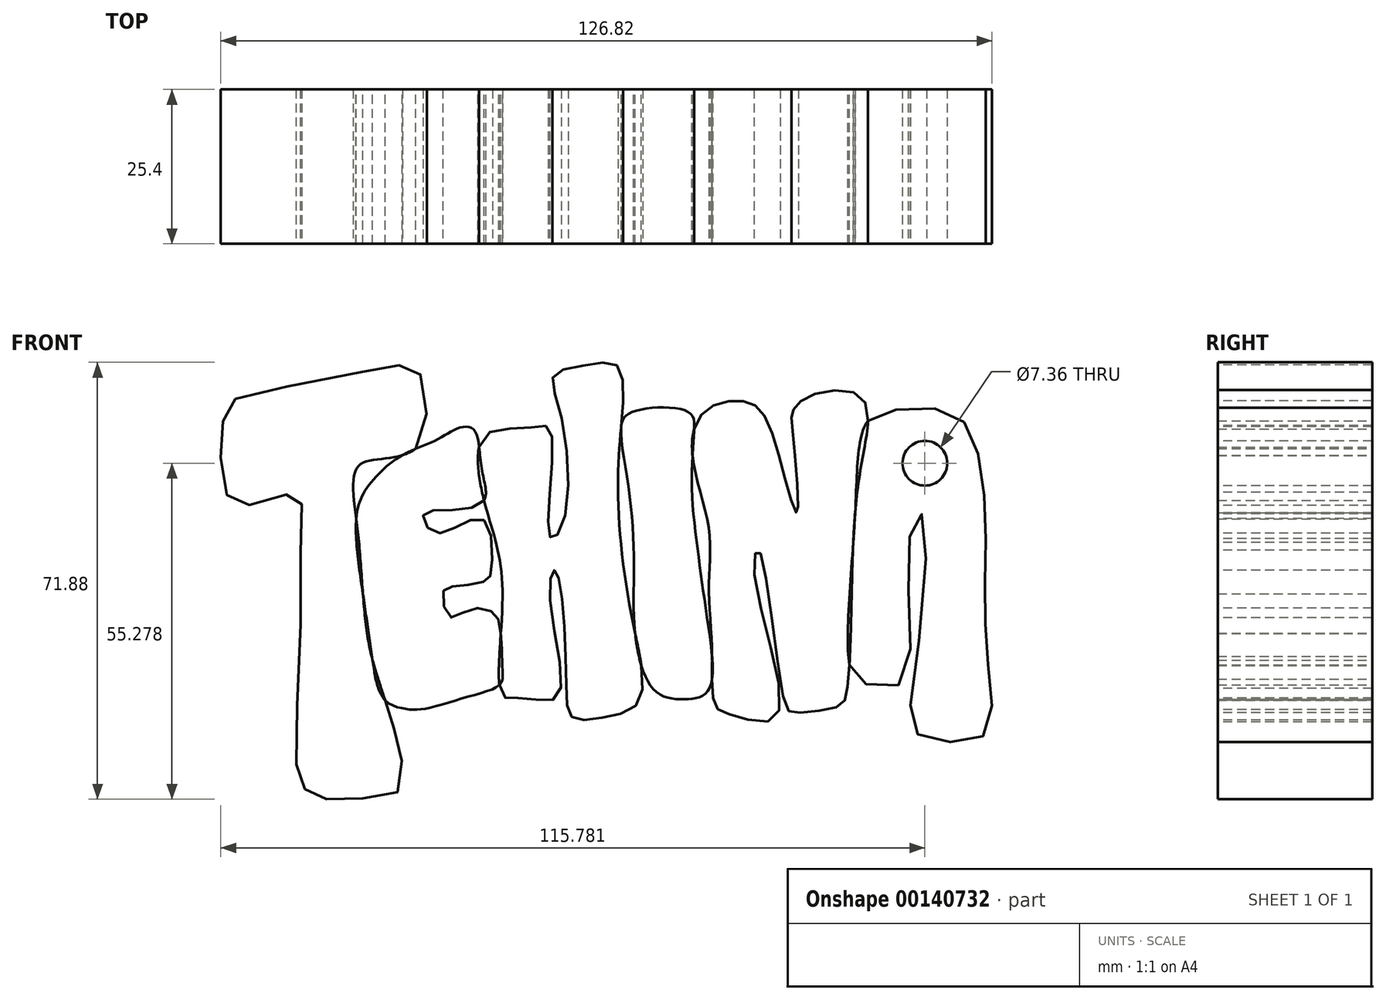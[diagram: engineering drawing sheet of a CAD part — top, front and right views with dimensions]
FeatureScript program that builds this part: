
annotation { "Feature Type Name" : "Feature", "Feature Type Description" : "" }
export const myFeature = defineFeature(function(context is Context, id is Id, definition is map)
    precondition{}
    {
        {
            var Q0;
            Q0=qCreatedBy(makeId("Front.planeOp"),FACE);
            var sketch = newSketch(context, id + "F0", { "sketchPlane" : qUnion([Q0])});
            skFitSpline(sketch, "E0", {"points": [v(-57.9, 25.8) * mm, v(-37.05, 29.96) * mm, v(-33.2, 30.6) * mm, v(-30.64, 30.12) * mm, v(-29.35, 25.47) * mm, v(-29.51, 18.25) * mm, v(-34.8, 15.37) * mm, v(-40.26, 13.92) * mm, v(-40.26, 3.02) * mm, v(-38.5, -15.02) * mm, v(-35.79, -24.54) * mm, v(-34.6, -28.44) * mm, v(-33.4, -31.84) * mm, v(-33.07, -37.89) * mm, v(-34.48, -40.11) * mm, v(-41.15, -40.72) * mm, v(-46, -40.72) * mm, v(-48.42, -39.7) * mm, v(-49.64, -38.1) * mm, v(-50.44, -33.85) * mm, v(-49.64, -10.61) * mm, v(-49.64, 6.16) * mm, v(-49.84, 9.6) * mm, v(-54.08, 8.58) * mm, v(-59.54, 7.57) * mm, v(-61.56, 8.79) * mm, v(-62.77, 14.44) * mm, v(-62.57, 20.5) * mm, v(-61.56, 24.14) * mm, v(-57.9, 25.8) * mm]});
            skFitSpline(sketch, "E1", {"points": [v(-27.4, 18.25) * mm, v(-23.57, 20.3) * mm, v(-21.15, 19.9) * mm, v(-19.93, 13.64) * mm, v(-19.53, 8.38) * mm, v(-24.98, 6.77) * mm, v(-29.51, 5.96) * mm, v(-27.81, 3.13) * mm, v(-23.37, 4.34) * mm, v(-19.33, 4.95) * mm, v(-18.32, -3.34) * mm, v(-19.33, -4.95) * mm, v(-24.18, -5.76) * mm, v(-26.2, -6.57) * mm, v(-25.19, -10.81) * mm, v(-21.95, -9.6) * mm, v(-18.11, -10) * mm, v(-16.9, -12.43) * mm, v(-16.5, -19.5) * mm, v(-16.9, -21.93) * mm, v(-22.16, -23.95) * mm, v(-29.51, -25.97) * mm, v(-32.26, -25.97) * mm, v(-35.79, -24.54) * mm, v(-37.85, -17.92) * mm, v(-39.44, -7.01) * mm, v(-40.54, 5.29) * mm, v(-38.5, 10.8) * mm, v(-32.97, 15.78) * mm, v(-27.4, 18.25) * mm]});
            skFitSpline(sketch, "E2", {"points": [v(-7, 22.93) * mm, v(-8.01, 29) * mm, v(-2.56, 30.6) * mm, v(2.3, 30.6) * mm, v(3.3, 24.14) * mm, v(2.5, 11.61) * mm, v(4.72, -10.61) * mm, v(5.93, -24.76) * mm, v(0, -27.38) * mm, v(-4.98, -27.38) * mm, v(-6, -22.13) * mm, v(-7, -5.76) * mm, v(-8.01, -3.14) * mm, v(-8.62, -8.6) * mm, v(-7.4, -23.95) * mm, v(-13.06, -24.15) * mm, v(-16.5, -23.75) * mm, v(-16.5, -5.96) * mm, v(-19.53, 8.38) * mm, v(-19.33, 19.1) * mm, v(-12.05, 20.3) * mm, v(-8.82, 20.3) * mm, v(-8.82, 8.38) * mm, v(-8.42, 2.12) * mm, v(-6.4, 4.95) * mm, v(-7, 22.93) * mm]});
            skFitSpline(sketch, "E3", {"points": [v(4.92, 22.93) * mm, v(3.02, 20.39) * mm, v(4.31, 10) * mm, v(5.12, -3.34) * mm, v(5.31, -13.5) * mm, v(8.56, -22.94) * mm, v(13.81, -24.35) * mm, v(17.45, -22.74) * mm, v(17.25, -11.62) * mm, v(15.63, 0) * mm, v(14.62, 11.41) * mm, v(15.02, 19.9) * mm, v(14.01, 22.93) * mm, v(4.92, 22.93) * mm]});
            skFitSpline(sketch, "E4", {"points": [v(16.64, 22.93) * mm, v(22.3, 24.75) * mm, v(26.14, 22.93) * mm, v(29.97, 11.82) * mm, v(32, 6.36) * mm, v(31.19, 19.9) * mm, v(31.19, 22.93) * mm, v(34.02, 25.56) * mm, v(42.5, 25.35) * mm, v(42.3, 13.03) * mm, v(40.89, -9) * mm, v(40.08, -23.54) * mm, v(38.66, -25.56) * mm, v(31.8, -26.57) * mm, v(29.97, -25.16) * mm, v(25.73, 0) * mm, v(24.92, -3.74) * mm, v(28.56, -27.18) * mm, v(21.29, -26.98) * mm, v(18.46, -25.36) * mm, v(17.97, -17.29) * mm, v(17.45, -5.36) * mm, v(17.45, 3.73) * mm, v(14.75, 15.73) * mm, v(16.64, 22.93) * mm]});
            skFitSpline(sketch, "E5", {"points": [v(43.6, 21.43) * mm, v(48.77, 23.33) * mm, v(57.05, 22.93) * mm, v(60.89, 18.69) * mm, v(62.7, 9.19) * mm, v(62.9, -2.13) * mm, v(62.9, -12.43) * mm, v(63.72, -22.13) * mm, v(63.11, -29.8) * mm, v(57.45, -31.42) * mm, v(51.4, -29.8) * mm, v(51.2, -20.71) * mm, v(52.6, 5.96) * mm, v(51.2, 5.15) * mm, v(50.38, -9.6) * mm, v(48.77, -21.93) * mm, v(42.9, -21.72) * mm, v(40.56, -18.67) * mm, v(41.5, 6.3) * mm, v(43.6, 21.43) * mm]});
            skSolve(sketch);
        }
        {
            var Q0;
            {var subQ0=sQuery(id+"F0.wireOp",EDGE,"E1");var subQ1=sQuery(id+"F0.wireOp",EDGE,"E0");var subQ7=makeQuery(id+"F0.imprint","INTERSECT",VERTEX,{"disambiguationData":[OD(2.0)],"derivedFrom":[subQ1,subQ0]});Q0=makeQuery(id+"F0.imprint","IMPRINT",FACE,{"disambiguationData":[TD([[makeQuery(id+"F0.imprint","IMPRINT",EDGE,{"disambiguationData":[TD([[subQ7,-1.0]])],"derivedFrom":subQ1}),-1.0]])]});}
            var Q1;
            Q1=sQuery(id+"F0.wireOp",EDGE,"E0");
            extrude(context, id + "F1", {"entities" : qUnion([Q0]), "surfaceEntities" : qUnion([Q1]), "depth" : 25.4 * mm});
        }
        {
            var Q0;
            {var subQ1=sQuery(id+"F0.wireOp",EDGE,"E1");var subQ4=sQuery(id+"F0.wireOp",EDGE,"E0");var subQ11=makeQuery(id+"F0.imprint","INTERSECT",VERTEX,{"disambiguationData":[OD(0.0)],"derivedFrom":[subQ4,subQ1]});Q0=makeQuery(id+"F0.imprint","IMPRINT",FACE,{"disambiguationData":[TD([[makeQuery(id+"F0.imprint","IMPRINT",EDGE,{"disambiguationData":[TD([[subQ11,-1.0]])],"derivedFrom":subQ4}),1.0]])]});}
            extrude(context, id + "F2", {"entities" : qUnion([Q0]), "depth" : 25.4 * mm});
        }
        {
            var Q0;
            {var subQ1=sQuery(id+"F0.wireOp",EDGE,"E2");var subQ4=sQuery(id+"F0.wireOp",EDGE,"E1");var subQ5=makeQuery(id+"F0.imprint","INTERSECT",VERTEX,{"disambiguationData":[OD(0.0)],"derivedFrom":[subQ4,subQ1]});Q0=makeQuery(id+"F0.imprint","IMPRINT",FACE,{"disambiguationData":[TD([[makeQuery(id+"F0.imprint","IMPRINT",EDGE,{"disambiguationData":[TD([[subQ5,-1.0]])],"derivedFrom":subQ4}),1.0]])]});}
            extrude(context, id + "F3", {"entities" : qUnion([Q0]), "depth" : 25.4 * mm});
        }
        {
            var Q0;
            {var subQ0=sQuery(id+"F0.wireOp",EDGE,"E3");var subQ1=sQuery(id+"F0.wireOp",EDGE,"E2");var subQ7=makeQuery(id+"F0.imprint","INTERSECT",VERTEX,{"disambiguationData":[OD(0.0)],"derivedFrom":[subQ1,subQ0]});Q0=makeQuery(id+"F0.imprint","IMPRINT",FACE,{"disambiguationData":[TD([[makeQuery(id+"F0.imprint","IMPRINT",EDGE,{"disambiguationData":[TD([[subQ7,-1.0]])],"derivedFrom":subQ1}),1.0]])]});}
            extrude(context, id + "F4", {"entities" : qUnion([Q0]), "depth" : 25.4 * mm});
        }
        {
            var Q0;
            {var subQ0=sQuery(id+"F0.wireOp",EDGE,"E4");var subQ1=sQuery(id+"F0.wireOp",EDGE,"E3");var subQ2=makeQuery(id+"F0.imprint","INTERSECT",VERTEX,{"disambiguationData":[OD(0.0)],"derivedFrom":[subQ1,subQ0]});Q0=makeQuery(id+"F0.imprint","IMPRINT",FACE,{"disambiguationData":[TD([[makeQuery(id+"F0.imprint","IMPRINT",EDGE,{"disambiguationData":[TD([[subQ2,-1.0]])],"derivedFrom":subQ1}),-1.0]])]});}
            extrude(context, id + "F5", {"entities" : qUnion([Q0]), "depth" : 25.4 * mm});
        }
        {
            var Q0;
            {var subQ0=sQuery(id+"F0.wireOp",EDGE,"E5");var subQ1=sQuery(id+"F0.wireOp",EDGE,"E4");var subQ2=makeQuery(id+"F0.imprint","INTERSECT",VERTEX,{"disambiguationData":[OD(0.0)],"derivedFrom":[subQ1,subQ0]});Q0=makeQuery(id+"F0.imprint","IMPRINT",FACE,{"disambiguationData":[TD([[makeQuery(id+"F0.imprint","IMPRINT",EDGE,{"disambiguationData":[TD([[subQ2,-1.0]])],"derivedFrom":subQ1}),1.0]])]});}
            extrude(context, id + "F6", {"entities" : qUnion([Q0]), "depth" : 25.4 * mm});
        }
        {
            var Q0;
            Q0=makeQuery(id+"F6.opExtrude","CAP_FACE",FACE,{"disambiguationData":[OSD([sQuery(id+"F0.wireOp",EDGE,"E4"),sQuery(id+"F0.wireOp",EDGE,"E5")])],"isStart":false});
            var sketch = newSketch(context, id + "F7", { "sketchPlane" : qUnion([Q0])});
            skCircle(sketch, "E6", {"center": v(52.96, 14.46) * mm, "radius": 3.68 * mm});
            skSolve(sketch);
        }
        {
            var Q0;
            Q0 = qSketchRegion(id + "F7", true);
            extrude(context, id + "F8", {"entities" : qUnion([Q0]), "operationType" : NewBodyOperationType.REMOVE, "oppositeDirection" : true, "depth" : 30.7 * mm});
        }
    });
